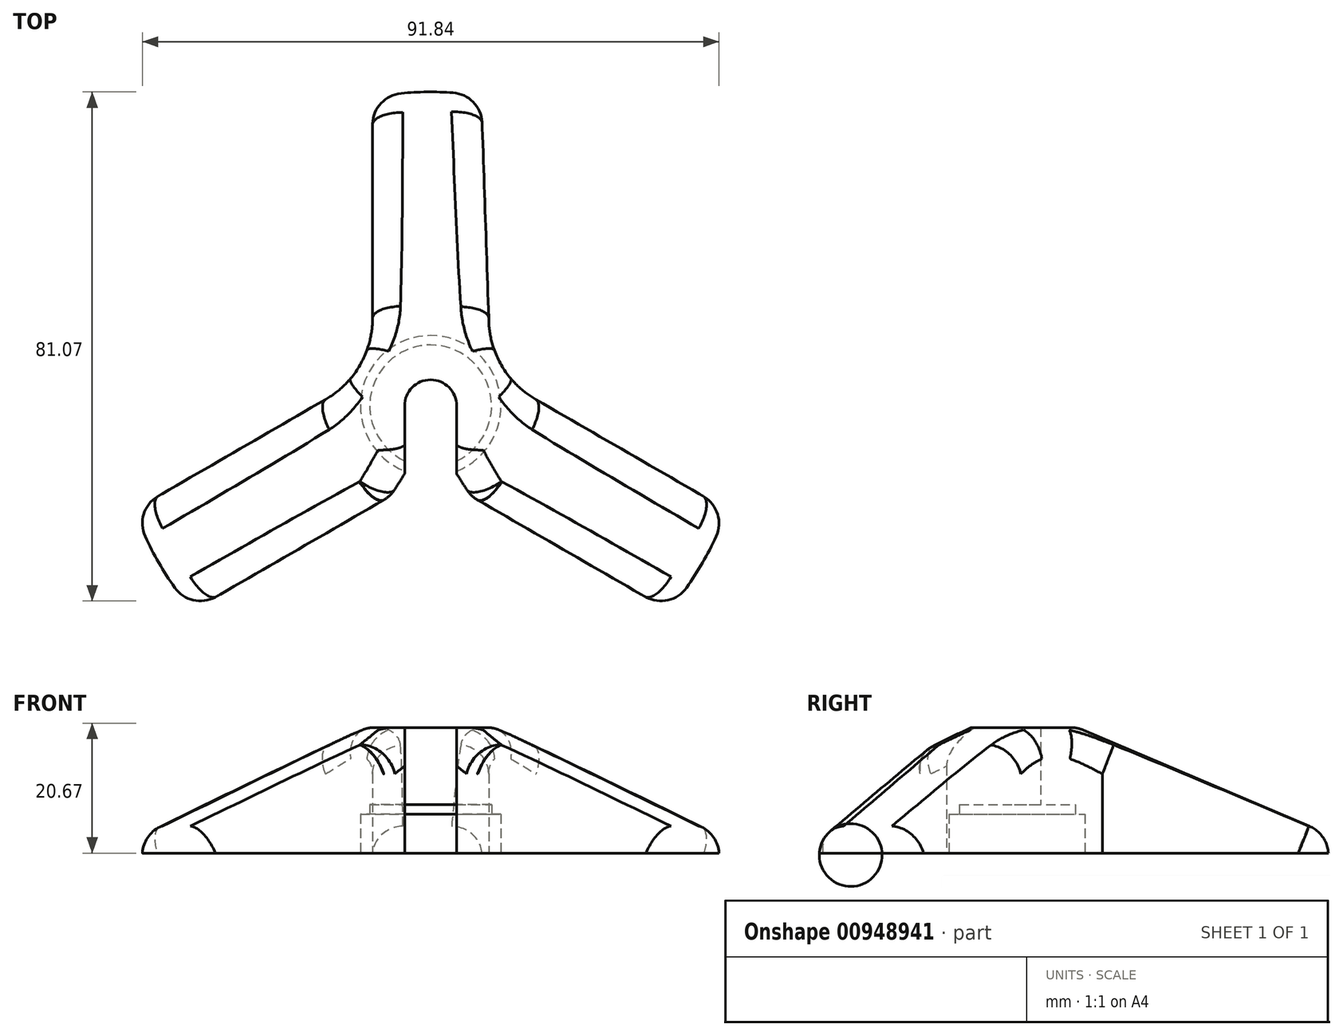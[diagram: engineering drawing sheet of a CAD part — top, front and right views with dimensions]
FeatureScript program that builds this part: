
annotation { "Feature Type Name" : "Feature", "Feature Type Description" : "" }
export const myFeature = defineFeature(function(context is Context, id is Id, definition is map)
    precondition{}
    {
        {
            assignVariable(context, id + "F0", {"name" : "Depth", "anyValue" : 40});
        }
        {
            var Q0;
            Q0=qCreatedBy(makeId("Front.planeOp"),FACE);
            var sketch = newSketch(context, id + "F1", { "sketchPlane" : qUnion([Q0])});
            skLineSegment(sketch, "E0", {"start": v(0, 0) * mm, "end": v(50, 0) * mm});
            skLineSegment(sketch, "E1", {"start": v(10, 20) * mm, "end": v(0, 20) * mm});
            skLineSegment(sketch, "E2", {"start": v(0, -6.9) * mm, "end": v(0, 21.2) * mm, "construction": true});
            skLineSegment(sketch, "E3", {"start": v(11.2, 0) * mm, "end": v(11.2, 6.2) * mm});
            skLineSegment(sketch, "E4", {"start": v(11.2, 6.2) * mm, "end": v(9.7, 6.2) * mm});
            skLineSegment(sketch, "E5", {"start": v(9.7, 6.2) * mm, "end": v(9.7, 7.7) * mm});
            skLineSegment(sketch, "E6", {"start": v(4.15, 7.7) * mm, "end": v(4.15, 20) * mm});
            skLineSegment(sketch, "E7", {"start": v(9.7, 7.7) * mm, "end": v(4.15, 7.7) * mm});
            skLineSegment(sketch, "E8", {"start": v(50, 0) * mm, "end": v(50, 3) * mm});
            skLineSegment(sketch, "E9", {"start": v(50, 3) * mm, "end": v(10, 20) * mm});
            skSolve(sketch);
        }
        {
            var Q0;
            {var subQ0=sQuery(id+"F1.wireOp",EDGE,"E3");Q0=makeQuery(id+"F1.imprint","IMPRINT",FACE,{"disambiguationData":[TD([[makeQuery(id+"F1.imprint","IMPRINT",EDGE,{"derivedFrom":subQ0}),-1.0]])]});}
            var Q1;
            Q1=sQuery(id+"F1.wireOp",EDGE,"E2");
            revolve(context, id + "F2", {"surfaceOperationType" : NewSurfaceOperationType.NEW, "entities" : qUnion([Q0]), "axis" : qUnion([Q1]), "revolveType" : RevolveType.FULL});
        }
        {
            var Q0;
            Q0=qCreatedBy(makeId("Top.planeOp"),FACE);
            var sketch = newSketch(context, id + "F3", { "sketchPlane" : qUnion([Q0])});
            skCircle(sketch, "E10", {"center": v(0, 0) * mm, "radius": 13 * mm, "construction": true});
            skCircle(sketch, "E11", {"center": v(0, 0) * mm, "radius": 50 * mm});
            skArc(sketch, "E12", {"start": v(9.25, 14) * mm, "mid": v(11.26, 6.5) * mm, "end": v(16.75, 1) * mm});
            skLineSegment(sketch, "E13", {"start": v(0, 0) * mm, "end": v(37.14, 21.44) * mm, "construction": true});
            skLineSegment(sketch, "E14", {"start": v(0, 0) * mm, "end": v(-44.06, 25.44) * mm, "construction": true});
            skLineSegment(sketch, "E15", {"start": v(0, 0) * mm, "end": v(0, -42.67) * mm, "construction": true});
            skArc(sketch, "E16", {"start": v(-16.75, 1) * mm, "mid": v(-11.26, 6.5) * mm, "end": v(-9.25, 14) * mm});
            skArc(sketch, "E17", {"start": v(7.5, -15) * mm, "mid": v(5.87, -14.2) * mm, "end": v(4.15, -13.59) * mm});
            skLineSegment(sketch, "E18", {"start": v(-9.25, 14) * mm, "end": v(-9.25, 49.14) * mm});
            skLineSegment(sketch, "E19.trimOffspring", {"start": v(9.25, 14) * mm, "end": v(8.05, 49.35) * mm});
            skLineSegment(sketch, "E20", {"start": v(0, 0) * mm, "end": v(-43.3, -25) * mm, "construction": true});
            skLineSegment(sketch, "E21", {"start": v(0, 0) * mm, "end": v(43.3, -25) * mm, "construction": true});
            skLineSegment(sketch, "E22", {"start": v(-47.18, -16.56) * mm, "end": v(-16.75, 1) * mm});
            skLineSegment(sketch, "E23", {"start": v(-37.93, -32.58) * mm, "end": v(-7.5, -15) * mm});
            skLineSegment(sketch, "E24", {"start": v(47.18, -16.56) * mm, "end": v(16.75, 1) * mm});
            skLineSegment(sketch, "E25", {"start": v(37.93, -32.58) * mm, "end": v(7.5, -15) * mm});
            skArc(sketch, "E26", {"start": v(3.6, -2.07) * mm, "mid": v(0, 4.15) * mm, "end": v(-3.6, -2.07) * mm});
            skLineSegment(sketch, "E27", {"start": v(-4.15, 0) * mm, "end": v(-4.15, -13.59) * mm});
            skLineSegment(sketch, "E28", {"start": v(4.15, 0) * mm, "end": v(4.15, -13.59) * mm});
            skArc(sketch, "E29.trimOffspring", {"start": v(-4.15, -13.59) * mm, "mid": v(-5.87, -14.2) * mm, "end": v(-7.5, -15) * mm});
            skSolve(sketch);
        }
        {
            var Q0;
            Q0=makeQuery(id+"F3.imprint","IMPRINT",FACE,{"disambiguationData":[TD([[makeQuery(id+"F3.imprint","IMPRINT",EDGE,{"derivedFrom":sQuery(id+"F3.wireOp",EDGE,"E17")}),1.0]])]});
            var Q1;
            Q1=makeQuery(id+"F3.imprint","IMPRINT",FACE,{"disambiguationData":[TD([[makeQuery(id+"F3.imprint","IMPRINT",EDGE,{"derivedFrom":sQuery(id+"F3.wireOp",EDGE,"E16")}),1.0]])]});
            var Q2;
            Q2=makeQuery(id+"F3.imprint","IMPRINT",FACE,{"disambiguationData":[TD([[makeQuery(id+"F3.imprint","IMPRINT",EDGE,{"derivedFrom":sQuery(id+"F3.wireOp",EDGE,"E12")}),1.0]])]});
            extrude(context, id + "F4", {"entities" : qUnion([Q0, Q1, Q2]), "operationType" : NewBodyOperationType.REMOVE, "depth" : (getVariable(context, 'Depth')) * mm, "offsetDistance" : 25 * mm});
        }
        {
            var Q0;
            Q0=makeQuery(id+"F4.boolean.opBoolean","COPY",EDGE,{"derivedFrom":makeQuery(id+"F4.opExtrude","SWEPT_EDGE",EDGE,{"disambiguationData":[OSD([sQuery(id+"F3.wireOp",EDGE,"E27"),sQuery(id+"F3.wireOp",EDGE,"E29.trimOffspring")])]})});
            var Q1;
            Q1=makeQuery(id+"F4.boolean.opBoolean","COPY",EDGE,{"derivedFrom":makeQuery(id+"F4.opExtrude","SWEPT_EDGE",EDGE,{"disambiguationData":[OSD([sQuery(id+"F3.wireOp",EDGE,"E17"),sQuery(id+"F3.wireOp",EDGE,"E28")])]})});
            chamfer(context, id + "F5", {"entities" : qUnion([Q0, Q1]), "width" : 4 * mm, "tangentPropagation" : true});
        }
        {
            var Q0;
            Q0=makeQuery(id+"F4.boolean.opBoolean","INTERSECT",EDGE,{"derivedFrom":[makeQuery(id+"F2.opRevolve","SWEPT_FACE",FACE,{"disambiguationData":[OSD([sQuery(id+"F1.wireOp",EDGE,"E9")])]}),makeQuery(id+"F4.opExtrude","SWEPT_FACE",FACE,{"disambiguationData":[OSD([sQuery(id+"F3.wireOp",EDGE,"E23")])]})]});
            var Q1;
            Q1=makeQuery(id+"F4.boolean.opBoolean","INTERSECT",EDGE,{"derivedFrom":[makeQuery(id+"F2.opRevolve","SWEPT_FACE",FACE,{"disambiguationData":[OSD([sQuery(id+"F1.wireOp",EDGE,"E9")])]}),makeQuery(id+"F4.opExtrude","SWEPT_FACE",FACE,{"disambiguationData":[OSD([sQuery(id+"F3.wireOp",EDGE,"E22")])]})]});
            var Q2;
            Q2=makeQuery(id+"F4.boolean.opBoolean","INTERSECT",EDGE,{"derivedFrom":[makeQuery(id+"F2.opRevolve","SWEPT_FACE",FACE,{"disambiguationData":[OSD([sQuery(id+"F1.wireOp",EDGE,"E9")])]}),makeQuery(id+"F4.opExtrude","SWEPT_FACE",FACE,{"disambiguationData":[OSD([sQuery(id+"F3.wireOp",EDGE,"E25")])]})]});
            var Q3;
            Q3=makeQuery(id+"F4.boolean.opBoolean","INTERSECT",EDGE,{"derivedFrom":[makeQuery(id+"F2.opRevolve","SWEPT_FACE",FACE,{"disambiguationData":[OSD([sQuery(id+"F1.wireOp",EDGE,"E9")])]}),makeQuery(id+"F4.opExtrude","SWEPT_FACE",FACE,{"disambiguationData":[OSD([sQuery(id+"F3.wireOp",EDGE,"E24")])]})]});
            var Q4;
            Q4=makeQuery(id+"F4.boolean.opBoolean","INTERSECT",EDGE,{"derivedFrom":[makeQuery(id+"F2.opRevolve","SWEPT_FACE",FACE,{"disambiguationData":[OSD([sQuery(id+"F1.wireOp",EDGE,"E9")])]}),makeQuery(id+"F4.opExtrude","SWEPT_FACE",FACE,{"disambiguationData":[OSD([sQuery(id+"F3.wireOp",EDGE,"E19.trimOffspring")])]})]});
            var Q5;
            {var subQ0=sQuery(id+"F1.wireOp",EDGE,"E8");var subQ1=sQuery(id+"F1.wireOp",EDGE,"E9");Q5=makeQuery(id+"F4.boolean.opBoolean","SPLIT",EDGE,{"disambiguationData":[TD([makeQuery(id+"F4.opExtrude","SWEPT_FACE",FACE,{"disambiguationData":[OSD([sQuery(id+"F3.wireOp",EDGE,"E22")])]})])],"derivedFrom":makeQuery(id+"F2.opRevolve","SWEPT_EDGE",EDGE,{"disambiguationData":[OSD([subQ0,subQ1])]})});}
            var Q6;
            {var subQ0=sQuery(id+"F1.wireOp",EDGE,"E8");var subQ1=sQuery(id+"F1.wireOp",EDGE,"E9");Q6=makeQuery(id+"F4.boolean.opBoolean","SPLIT",EDGE,{"disambiguationData":[TD([makeQuery(id+"F4.opExtrude","SWEPT_FACE",FACE,{"disambiguationData":[OSD([sQuery(id+"F3.wireOp",EDGE,"E24")])]})])],"derivedFrom":makeQuery(id+"F2.opRevolve","SWEPT_EDGE",EDGE,{"disambiguationData":[OSD([subQ0,subQ1])]})});}
            var Q7;
            {var subQ0=sQuery(id+"F1.wireOp",EDGE,"E8");var subQ1=sQuery(id+"F1.wireOp",EDGE,"E9");Q7=makeQuery(id+"F4.boolean.opBoolean","SPLIT",EDGE,{"disambiguationData":[TD([makeQuery(id+"F4.opExtrude","SWEPT_FACE",FACE,{"disambiguationData":[OSD([sQuery(id+"F3.wireOp",EDGE,"E18")])]})])],"derivedFrom":makeQuery(id+"F2.opRevolve","SWEPT_EDGE",EDGE,{"disambiguationData":[OSD([subQ0,subQ1])]})});}
            fillet(context, id + "F6", {"entities" : qUnion([Q0, Q1, Q2, Q3, Q4, Q5, Q6, Q7]), "radius" : 5 * mm, "tangentPropagation" : true, "allowEdgeOverflow" : false});
        }
        {
            var Q0;
            {var subQ0=sQuery(id+"F1.wireOp",EDGE,"E8");var subQ1=makeQuery(id+"F4.opExtrude","SWEPT_FACE",FACE,{"disambiguationData":[OSD([sQuery(id+"F3.wireOp",EDGE,"E19.trimOffspring")])]});var subQ2=sQuery(id+"F1.wireOp",EDGE,"E9");var subQ3=makeQuery(id+"F2.opRevolve","SWEPT_FACE",FACE,{"disambiguationData":[OSD([subQ2])]});Q0=makeQuery(id+"F6.opFillet","BLEND_EDGE",EDGE,{"blendedFrom":[makeQuery(id+"F4.boolean.opBoolean","INTERSECT",EDGE,{"derivedFrom":[subQ3,subQ1]}),makeQuery(id+"F4.boolean.opBoolean","SPLIT",EDGE,{"disambiguationData":[TD([makeQuery(id+"F4.opExtrude","SWEPT_FACE",FACE,{"disambiguationData":[OSD([sQuery(id+"F3.wireOp",EDGE,"E18")])]})])],"derivedFrom":makeQuery(id+"F2.opRevolve","SWEPT_EDGE",EDGE,{"disambiguationData":[OSD([subQ0,subQ2])]})})],"blendedInto":[]});}
            var Q1;
            {var subQ0=sQuery(id+"F1.wireOp",EDGE,"E8");var subQ1=sQuery(id+"F1.wireOp",EDGE,"E9");var subQ2=makeQuery(id+"F2.opRevolve","SWEPT_FACE",FACE,{"disambiguationData":[OSD([subQ1])]});var subQ3=makeQuery(id+"F4.opExtrude","SWEPT_FACE",FACE,{"disambiguationData":[OSD([sQuery(id+"F3.wireOp",EDGE,"E18")])]});Q1=makeQuery(id+"F6.opFillet","BLEND_EDGE",EDGE,{"blendedFrom":[makeQuery(id+"F4.boolean.opBoolean","INTERSECT",EDGE,{"derivedFrom":[subQ2,subQ3]}),makeQuery(id+"F4.boolean.opBoolean","SPLIT",EDGE,{"disambiguationData":[TD([subQ3])],"derivedFrom":makeQuery(id+"F2.opRevolve","SWEPT_EDGE",EDGE,{"disambiguationData":[OSD([subQ0,subQ1])]})})],"blendedInto":[]});}
            var Q2;
            {var subQ0=sQuery(id+"F1.wireOp",EDGE,"E8");var subQ1=sQuery(id+"F1.wireOp",EDGE,"E9");var subQ2=makeQuery(id+"F2.opRevolve","SWEPT_FACE",FACE,{"disambiguationData":[OSD([subQ1])]});var subQ3=makeQuery(id+"F4.opExtrude","SWEPT_FACE",FACE,{"disambiguationData":[OSD([sQuery(id+"F3.wireOp",EDGE,"E22")])]});Q2=makeQuery(id+"F6.opFillet","BLEND_EDGE",EDGE,{"blendedFrom":[makeQuery(id+"F4.boolean.opBoolean","INTERSECT",EDGE,{"derivedFrom":[subQ2,subQ3]}),makeQuery(id+"F4.boolean.opBoolean","SPLIT",EDGE,{"disambiguationData":[TD([subQ3])],"derivedFrom":makeQuery(id+"F2.opRevolve","SWEPT_EDGE",EDGE,{"disambiguationData":[OSD([subQ0,subQ1])]})})],"blendedInto":[]});}
            var Q3;
            {var subQ0=sQuery(id+"F1.wireOp",EDGE,"E8");var subQ1=sQuery(id+"F1.wireOp",EDGE,"E9");var subQ2=makeQuery(id+"F2.opRevolve","SWEPT_FACE",FACE,{"disambiguationData":[OSD([subQ1])]});var subQ3=makeQuery(id+"F4.opExtrude","SWEPT_FACE",FACE,{"disambiguationData":[OSD([sQuery(id+"F3.wireOp",EDGE,"E23")])]});Q3=makeQuery(id+"F6.opFillet","BLEND_EDGE",EDGE,{"blendedFrom":[makeQuery(id+"F4.boolean.opBoolean","INTERSECT",EDGE,{"derivedFrom":[subQ2,subQ3]}),makeQuery(id+"F4.boolean.opBoolean","SPLIT",EDGE,{"disambiguationData":[TD([makeQuery(id+"F4.opExtrude","SWEPT_FACE",FACE,{"disambiguationData":[OSD([sQuery(id+"F3.wireOp",EDGE,"E22")])]})])],"derivedFrom":makeQuery(id+"F2.opRevolve","SWEPT_EDGE",EDGE,{"disambiguationData":[OSD([subQ0,subQ1])]})})],"blendedInto":[]});}
            var Q4;
            {var subQ0=sQuery(id+"F1.wireOp",EDGE,"E8");var subQ1=sQuery(id+"F1.wireOp",EDGE,"E9");var subQ2=makeQuery(id+"F2.opRevolve","SWEPT_FACE",FACE,{"disambiguationData":[OSD([subQ1])]});var subQ3=makeQuery(id+"F4.opExtrude","SWEPT_FACE",FACE,{"disambiguationData":[OSD([sQuery(id+"F3.wireOp",EDGE,"E24")])]});Q4=makeQuery(id+"F6.opFillet","BLEND_EDGE",EDGE,{"blendedFrom":[makeQuery(id+"F4.boolean.opBoolean","INTERSECT",EDGE,{"derivedFrom":[subQ2,subQ3]}),makeQuery(id+"F4.boolean.opBoolean","SPLIT",EDGE,{"disambiguationData":[TD([subQ3])],"derivedFrom":makeQuery(id+"F2.opRevolve","SWEPT_EDGE",EDGE,{"disambiguationData":[OSD([subQ0,subQ1])]})})],"blendedInto":[]});}
            var Q5;
            {var subQ0=sQuery(id+"F1.wireOp",EDGE,"E8");var subQ1=sQuery(id+"F1.wireOp",EDGE,"E9");var subQ2=makeQuery(id+"F2.opRevolve","SWEPT_FACE",FACE,{"disambiguationData":[OSD([subQ1])]});var subQ3=makeQuery(id+"F4.opExtrude","SWEPT_FACE",FACE,{"disambiguationData":[OSD([sQuery(id+"F3.wireOp",EDGE,"E25")])]});Q5=makeQuery(id+"F6.opFillet","BLEND_EDGE",EDGE,{"blendedFrom":[makeQuery(id+"F4.boolean.opBoolean","INTERSECT",EDGE,{"derivedFrom":[subQ2,subQ3]}),makeQuery(id+"F4.boolean.opBoolean","SPLIT",EDGE,{"disambiguationData":[TD([makeQuery(id+"F4.opExtrude","SWEPT_FACE",FACE,{"disambiguationData":[OSD([sQuery(id+"F3.wireOp",EDGE,"E24")])]})])],"derivedFrom":makeQuery(id+"F2.opRevolve","SWEPT_EDGE",EDGE,{"disambiguationData":[OSD([subQ0,subQ1])]})})],"blendedInto":[]});}
            var Q6;
            {var subQ0=sQuery(id+"F3.wireOp",EDGE,"E29.trimOffspring");Q6=makeQuery(id+"F5.opChamfer","BLEND_EDGE",EDGE,{"blendedFrom":[makeQuery(id+"F4.boolean.opBoolean","COPY",EDGE,{"derivedFrom":makeQuery(id+"F4.opExtrude","SWEPT_EDGE",EDGE,{"disambiguationData":[OSD([sQuery(id+"F3.wireOp",EDGE,"E27"),subQ0])]})}),makeQuery(id+"F4.boolean.opBoolean","COPY",FACE,{"derivedFrom":makeQuery(id+"F4.opExtrude","SWEPT_FACE",FACE,{"disambiguationData":[OSD([subQ0])]})})],"blendedInto":[makeQuery(id+"F4.boolean.opBoolean","COPY",FACE,{"derivedFrom":makeQuery(id+"F4.opExtrude","SWEPT_FACE",FACE,{"disambiguationData":[OSD([subQ0])]})})]});}
            var Q7;
            {var subQ0=sQuery(id+"F3.wireOp",EDGE,"E17");Q7=makeQuery(id+"F5.opChamfer","BLEND_EDGE",EDGE,{"blendedFrom":[makeQuery(id+"F4.boolean.opBoolean","COPY",EDGE,{"derivedFrom":makeQuery(id+"F4.opExtrude","SWEPT_EDGE",EDGE,{"disambiguationData":[OSD([subQ0,sQuery(id+"F3.wireOp",EDGE,"E28")])]})}),makeQuery(id+"F4.boolean.opBoolean","COPY",FACE,{"derivedFrom":makeQuery(id+"F4.opExtrude","SWEPT_FACE",FACE,{"disambiguationData":[OSD([subQ0])]})})],"blendedInto":[makeQuery(id+"F4.boolean.opBoolean","COPY",FACE,{"derivedFrom":makeQuery(id+"F4.opExtrude","SWEPT_FACE",FACE,{"disambiguationData":[OSD([subQ0])]})})]});}
            var Q8;
            Q8=makeQuery(id+"F4.boolean.opBoolean","COPY",EDGE,{"derivedFrom":makeQuery(id+"F4.opExtrude","SWEPT_EDGE",EDGE,{"disambiguationData":[OSD([sQuery(id+"F3.wireOp",EDGE,"E17"),sQuery(id+"F3.wireOp",EDGE,"E25")])]})});
            var Q9;
            Q9=makeQuery(id+"F4.boolean.opBoolean","COPY",EDGE,{"derivedFrom":makeQuery(id+"F4.opExtrude","SWEPT_EDGE",EDGE,{"disambiguationData":[OSD([sQuery(id+"F3.wireOp",EDGE,"E23"),sQuery(id+"F3.wireOp",EDGE,"E29.trimOffspring")])]})});
            var Q10;
            Q10=makeQuery(id+"F2.opRevolve","SWEPT_EDGE",EDGE,{"disambiguationData":[OSD([sQuery(id+"F1.wireOp",EDGE,"E1"),sQuery(id+"F1.wireOp",EDGE,"E9")])]});
            var Q11;
            Q11=makeQuery(id+"F2.opRevolve","SWEPT_EDGE",EDGE,{"disambiguationData":[OSD([sQuery(id+"F1.wireOp",EDGE,"E1"),sQuery(id+"F1.wireOp",EDGE,"E9")])]});
            fillet(context, id + "F7", {"entities" : qUnion([Q0, Q1, Q2, Q3, Q4, Q5, Q6, Q7, Q8, Q9, Q10, Q11]), "radius" : 5 * mm, "tangentPropagation" : true, "allowEdgeOverflow" : false});
        }
    });
